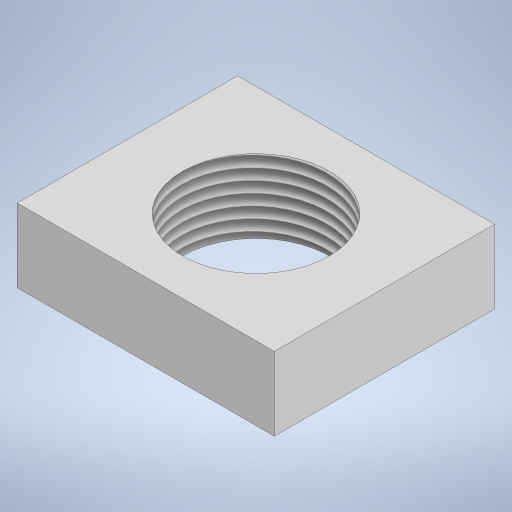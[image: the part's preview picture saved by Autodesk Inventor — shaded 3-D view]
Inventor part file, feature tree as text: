
AUTODESK INVENTOR PART (.ipt)
format: ipt  version: 2023 (Build 270158000, 158)  size: 224,256 bytes
history: native  units: mm
features: other x1, extrude x1, thread x1, sketch x1
ambient origin geometry x8: Origin, YZ Plane, XZ Plane, XY Plane, X Axis, Y Axis, Z Axis, Center Point
bodies: Body1 (feature_tree)
feature tree (4):
  other  "Твердое тело1"
  extrude  "Выдавливание1"  Depth=35.0mm
  thread  "Резьба2"
  sketch  "Эскиз1"
